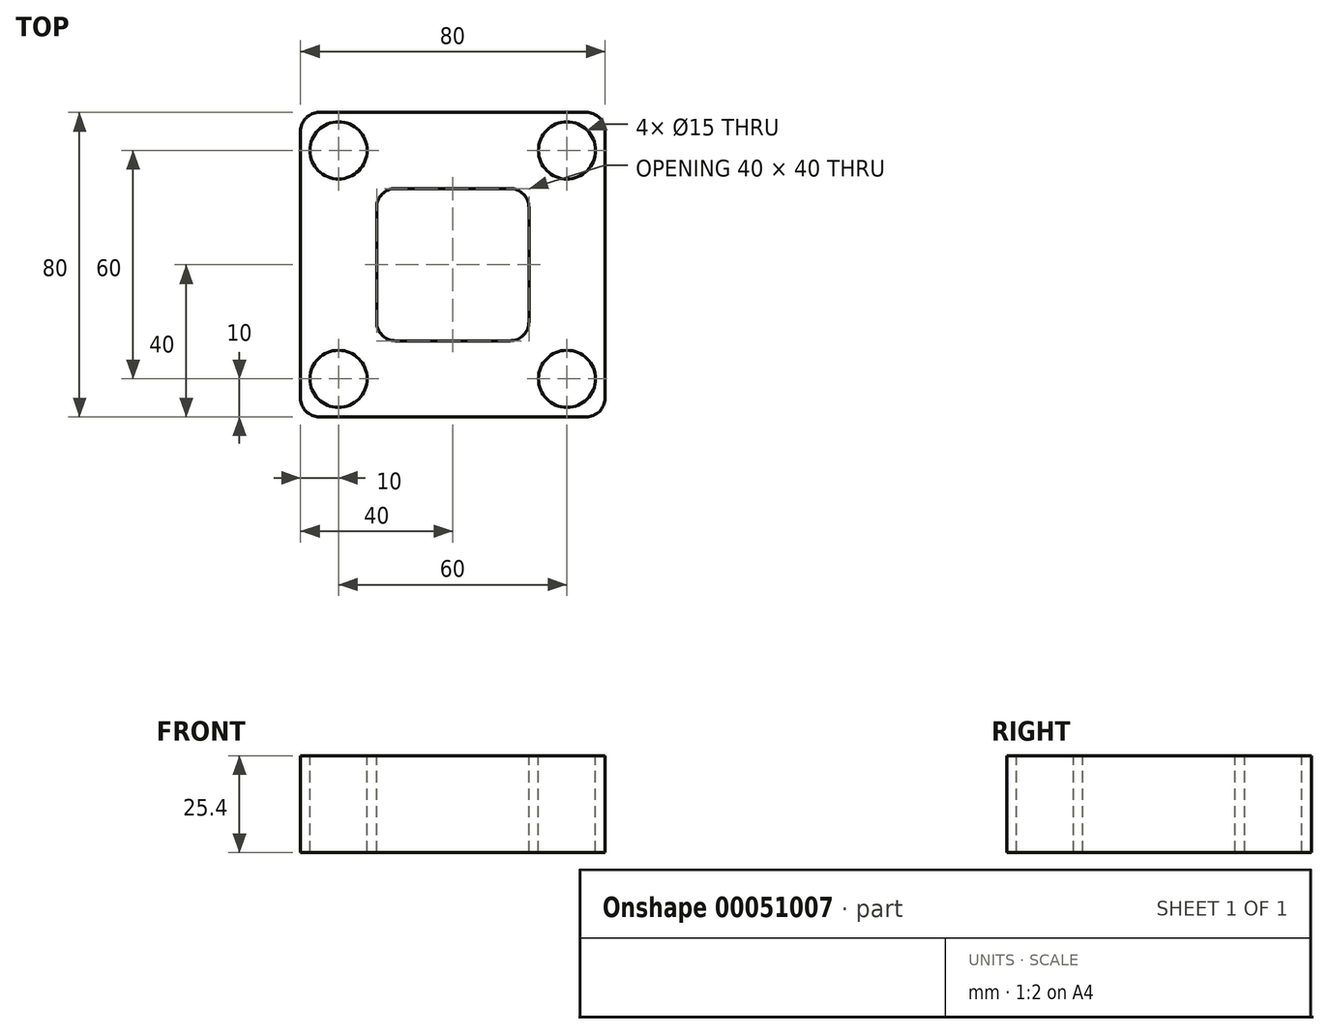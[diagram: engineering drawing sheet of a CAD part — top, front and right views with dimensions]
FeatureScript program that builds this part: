
annotation { "Feature Type Name" : "Feature", "Feature Type Description" : "" }
export const myFeature = defineFeature(function(context is Context, id is Id, definition is map)
    precondition{}
    {
        {
            var Q0;
            Q0=qCreatedBy(makeId("Top.planeOp"),FACE);
            var sketch = newSketch(context, id + "F0", { "sketchPlane" : qUnion([Q0])});
            skLineSegment(sketch, "E0", {"start": v(-40, -40) * mm, "end": v(40, -40) * mm});
            skLineSegment(sketch, "E1", {"start": v(40, -40) * mm, "end": v(40, 40) * mm});
            skLineSegment(sketch, "E2", {"start": v(40, 40) * mm, "end": v(-40, 40) * mm});
            skLineSegment(sketch, "E3", {"start": v(-40, 40) * mm, "end": v(-40, -40) * mm});
            skLineSegment(sketch, "E4", {"start": v(0, 48.84) * mm, "end": v(0, -45.6) * mm, "construction": true});
            skLineSegment(sketch, "E5", {"start": v(-43.87, 0) * mm, "end": v(44.8, 0) * mm, "construction": true});
            skPoint(sketch, "E5.startSnap0", {"position": v(-40, 0) * mm});
            skSolve(sketch);
        }
        {
            var Q0;
            Q0 = qSketchRegion(id + "F0", true);
            extrude(context, id + "F1", {"entities" : qUnion([Q0]), "depth" : 25.4 * mm});
        }
        {
            var Q0;
            Q0=makeQuery(id+"F1.opExtrude","CAP_FACE",FACE,{"disambiguationData":[OSD([sQuery(id+"F0.wireOp",EDGE,"E0"),sQuery(id+"F0.wireOp",EDGE,"E1"),sQuery(id+"F0.wireOp",EDGE,"E2"),sQuery(id+"F0.wireOp",EDGE,"E3")])],"isStart":false});
            var sketch = newSketch(context, id + "F2", { "sketchPlane" : qUnion([Q0])});
            skLineSegment(sketch, "E6.rect.bottom", {"start": v(-20, 20) * mm, "end": v(20, 20) * mm});
            skLineSegment(sketch, "E6.rect.top", {"start": v(-20, -20) * mm, "end": v(20, -20) * mm});
            skLineSegment(sketch, "E6.rect.left", {"start": v(-20, 20) * mm, "end": v(-20, -20) * mm});
            skLineSegment(sketch, "E6.rect.right", {"start": v(20, 20) * mm, "end": v(20, -20) * mm});
            skPoint(sketch, "E6.rect.middle", {"position": v(0, 0) * mm});
            skSolve(sketch);
        }
        {
            var Q0;
            Q0 = qSketchRegion(id + "F2", true);
            extrude(context, id + "F3", {"entities" : qUnion([Q0]), "operationType" : NewBodyOperationType.REMOVE, "oppositeDirection" : true, "depth" : 25.4 * mm});
        }
        {
            var Q0;
            Q0=makeQuery(id+"F1.opExtrude","CAP_FACE",FACE,{"disambiguationData":[OSD([sQuery(id+"F0.wireOp",EDGE,"E0"),sQuery(id+"F0.wireOp",EDGE,"E1"),sQuery(id+"F0.wireOp",EDGE,"E2"),sQuery(id+"F0.wireOp",EDGE,"E3")])],"isStart":false});
            var sketch = newSketch(context, id + "F4", { "sketchPlane" : qUnion([Q0])});
            skLineSegment(sketch, "E7", {"start": v(-30, 30) * mm, "end": v(30, 30) * mm});
            skLineSegment(sketch, "E8", {"start": v(30, 30) * mm, "end": v(30, -30) * mm});
            skLineSegment(sketch, "E9", {"start": v(30, -30) * mm, "end": v(-30, -30) * mm});
            skLineSegment(sketch, "E10", {"start": v(-30, 30) * mm, "end": v(-30, -30) * mm});
            skSolve(sketch);
        }
        {
            var Q0;
            Q0=sQuery(id+"F4.wireOp",VERTEX,"E9.end");
            var Q1;
            Q1=sQuery(id+"F4.wireOp",VERTEX,"E9.start");
            var Q2;
            Q2=sQuery(id+"F4.wireOp",VERTEX,"E8.start");
            var Q3;
            Q3=sQuery(id+"F4.wireOp",VERTEX,"E10.start");
            var Q4;
            Q4=makeQuery(id+"F1.opExtrude","SWEPT_BODY",BODY,{"disambiguationData":[OSD([sQuery(id+"F0.wireOp",EDGE,"E0"),sQuery(id+"F0.wireOp",EDGE,"E1"),sQuery(id+"F0.wireOp",EDGE,"E2"),sQuery(id+"F0.wireOp",EDGE,"E3")])]});
            hole(context, id + "F5", {"style" : HoleStyle.SIMPLE, "holeDiameter" : 15 * mm, "endStyle" : HoleEndStyle.THROUGH, "locations" : qUnion([Q0, Q1, Q2, Q3]), "scope" : qUnion([Q4])});
        }
        {
            var Q0;
            Q0=makeQuery(id+"F1.opExtrude","SWEPT_EDGE",EDGE,{"disambiguationData":[OSD([sQuery(id+"F0.wireOp",EDGE,"E0"),sQuery(id+"F0.wireOp",EDGE,"E1")])]});
            var Q1;
            Q1=makeQuery(id+"F1.opExtrude","SWEPT_EDGE",EDGE,{"disambiguationData":[OSD([sQuery(id+"F0.wireOp",EDGE,"E0"),sQuery(id+"F0.wireOp",EDGE,"E3")])]});
            var Q2;
            Q2=makeQuery(id+"F1.opExtrude","SWEPT_EDGE",EDGE,{"disambiguationData":[OSD([sQuery(id+"F0.wireOp",EDGE,"E1"),sQuery(id+"F0.wireOp",EDGE,"E2")])]});
            var Q3;
            Q3=makeQuery(id+"F1.opExtrude","SWEPT_EDGE",EDGE,{"disambiguationData":[OSD([sQuery(id+"F0.wireOp",EDGE,"E2"),sQuery(id+"F0.wireOp",EDGE,"E3")])]});
            fillet(context, id + "F6", {"entities" : qUnion([Q0, Q1, Q2, Q3]), "radius" : 5 * mm, "tangentPropagation" : true, "allowEdgeOverflow" : false});
        }
        {
            var Q0;
            Q0=makeQuery(id+"F3.boolean.opBoolean","COPY",EDGE,{"derivedFrom":makeQuery(id+"F3.opExtrude","SWEPT_EDGE",EDGE,{"disambiguationData":[OSD([sQuery(id+"F2.wireOp",EDGE,"E6.rect.bottom"),sQuery(id+"F2.wireOp",EDGE,"E6.rect.left")])]})});
            var Q1;
            Q1=makeQuery(id+"F3.boolean.opBoolean","COPY",EDGE,{"derivedFrom":makeQuery(id+"F3.opExtrude","SWEPT_EDGE",EDGE,{"disambiguationData":[OSD([sQuery(id+"F2.wireOp",EDGE,"E6.rect.top"),sQuery(id+"F2.wireOp",EDGE,"E6.rect.left")])]})});
            var Q2;
            Q2=makeQuery(id+"F3.boolean.opBoolean","COPY",EDGE,{"derivedFrom":makeQuery(id+"F3.opExtrude","SWEPT_EDGE",EDGE,{"disambiguationData":[OSD([sQuery(id+"F2.wireOp",EDGE,"E6.rect.bottom"),sQuery(id+"F2.wireOp",EDGE,"E6.rect.right")])]})});
            var Q3;
            Q3=makeQuery(id+"F3.boolean.opBoolean","COPY",EDGE,{"derivedFrom":makeQuery(id+"F3.opExtrude","SWEPT_EDGE",EDGE,{"disambiguationData":[OSD([sQuery(id+"F2.wireOp",EDGE,"E6.rect.top"),sQuery(id+"F2.wireOp",EDGE,"E6.rect.right")])]})});
            fillet(context, id + "F7", {"entities" : qUnion([Q0, Q1, Q2, Q3]), "radius" : 5 * mm, "tangentPropagation" : true, "allowEdgeOverflow" : false});
        }
    });
